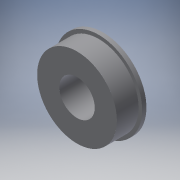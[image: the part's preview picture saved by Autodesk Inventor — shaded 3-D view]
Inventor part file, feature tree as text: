
AUTODESK INVENTOR PART (.ipt)
format: ipt  version: 2016 (Build 200138000, 138)  size: 110,080 bytes
history: native  units: in
note: dims shown in document units (in); Inventor stores cm internally (conversion verified against a paired STEP export)
features: extrude x2, sketch x2
ambient origin geometry x8: Origin, YZ Plane, XZ Plane, XY Plane, X Axis, Y Axis, Z Axis, Center Point
bodies: Solid1 (feature_tree)
feature tree (4):
  extrude  "Extrusion1"  Depth=0.5in
  extrude  "Extrusion2"  Depth=0.06in
  sketch  "Sketch1"  dims[d0=1.125in d1=0.5in]
  sketch  "Sketch2"  dims[d2=0.306in d3=0.0in d4=1.225in d5=0.5in d6=0.06in d7=0.0in]
